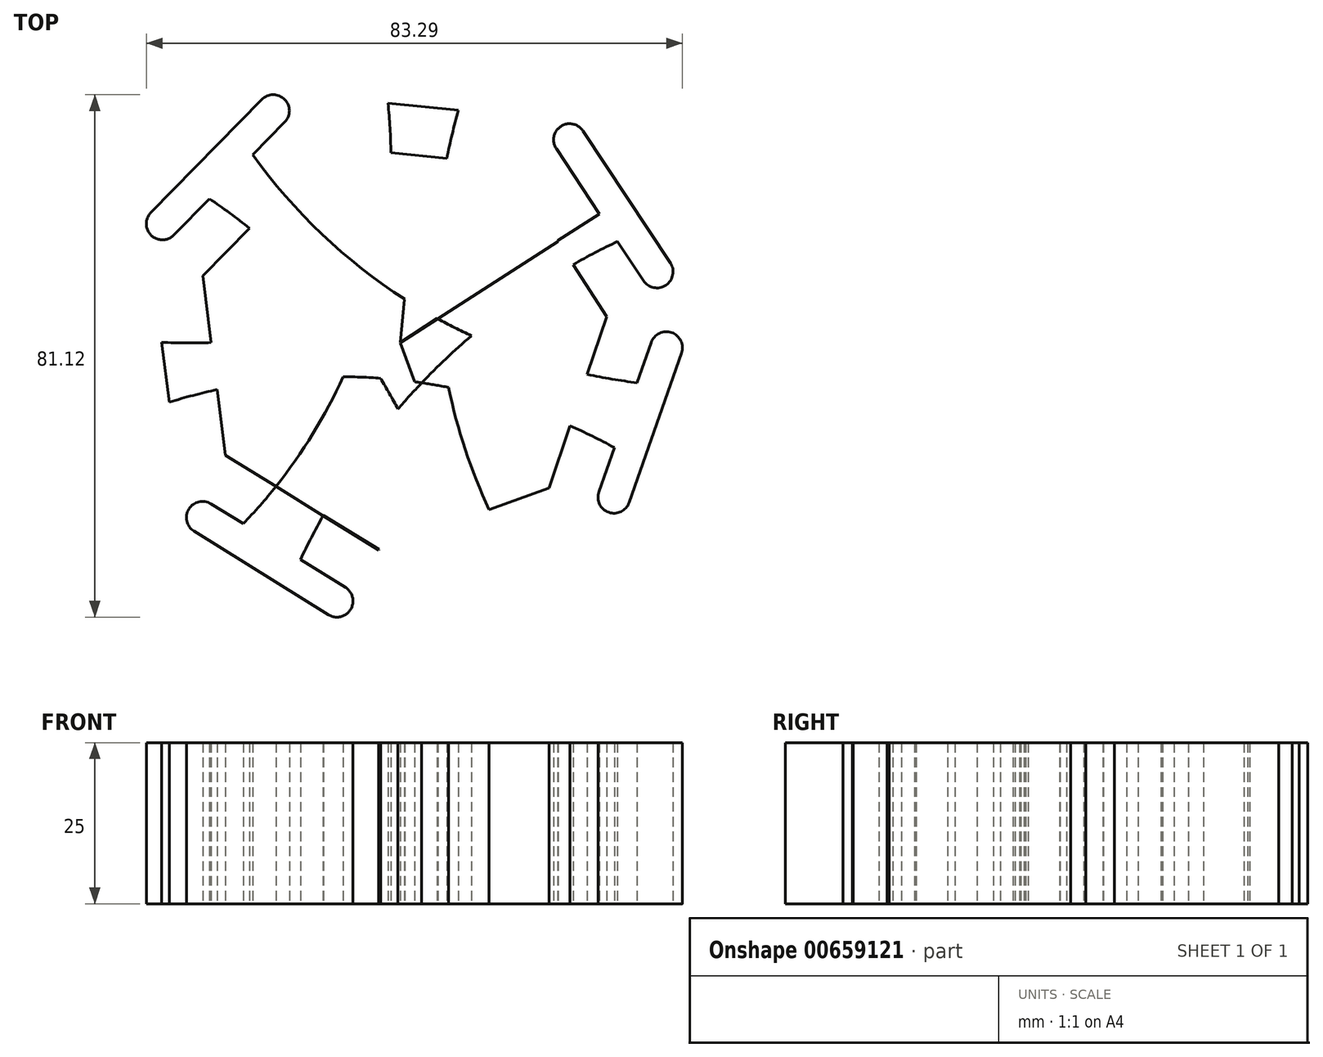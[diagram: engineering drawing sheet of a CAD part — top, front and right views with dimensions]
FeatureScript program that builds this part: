
annotation { "Feature Type Name" : "Feature", "Feature Type Description" : "" }
export const myFeature = defineFeature(function(context is Context, id is Id, definition is map)
    precondition{}
    {
        {
            var Q0;
            Q0=qCreatedBy(makeId("Top.planeOp"),FACE);
            var sketch = newSketch(context, id + "F0", { "sketchPlane" : qUnion([Q0])});
            skCircle(sketch, "E0.cCircle", {"center": v(0, 0) * mm, "radius": 29.14 * mm, "construction": true});
            skLineSegment(sketch, "E0.0", {"start": v(16.9, 27.58) * mm, "end": v(32.1, 3.99) * mm});
            skLineSegment(sketch, "E0.1", {"start": v(32.1, 3.99) * mm, "end": v(23.12, -22.6) * mm});
            skLineSegment(sketch, "E0.2", {"start": v(23.12, -22.6) * mm, "end": v(-3.25, -32.17) * mm});
            skLineSegment(sketch, "E0.3", {"start": v(-3.25, -32.17) * mm, "end": v(-27.18, -17.52) * mm});
            skLineSegment(sketch, "E0.4", {"start": v(-27.18, -17.52) * mm, "end": v(-30.64, 10.33) * mm});
            skLineSegment(sketch, "E0.5", {"start": v(-30.64, 10.33) * mm, "end": v(-11.03, 30.4) * mm});
            skLineSegment(sketch, "E0.6", {"start": v(-11.03, 30.4) * mm, "end": v(16.9, 27.58) * mm});
            skPoint(sketch, "E0.0.midPoint", {"position": v(24.5, 15.78) * mm});
            skLineSegment(sketch, "E1", {"start": v(23.12, -22.6) * mm, "end": v(27.6, -9.3) * mm});
            skLineSegment(sketch, "E2", {"start": v(-3.25, -32.17) * mm, "end": v(23.12, -22.6) * mm});
            skLineSegment(sketch, "E3", {"start": v(0, 0) * mm, "end": v(2.93, 28.99) * mm});
            skLineSegment(sketch, "E4", {"start": v(2.93, 28.99) * mm, "end": v(3.94, 38.94) * mm});
            skLineSegment(sketch, "E5.0", {"start": v(-7.82, 40.24) * mm, "end": v(16.63, 37.77) * mm});
            skArc(sketch, "E6.0.startCap", {"start": v(-8.07, 37.75) * mm, "mid": v(-10.3, 40.5) * mm, "end": v(-7.56, 42.73) * mm});
            skArc(sketch, "E6.0.endCap", {"start": v(16.89, 40.25) * mm, "mid": v(19.12, 37.51) * mm, "end": v(16.38, 35.28) * mm});
            skLineSegment(sketch, "E6.0.left", {"start": v(-7.56, 42.73) * mm, "end": v(16.89, 40.25) * mm});
            skLineSegment(sketch, "E6.0.right", {"start": v(-8.07, 37.75) * mm, "end": v(16.38, 35.28) * mm});
            skLineSegment(sketch, "E7.MirrorCS", {"start": v(-17.93, 34.19) * mm, "end": v(-35.15, 16.66) * mm});
            skLineSegment(sketch, "E8.MirrorCS", {"start": v(-20.78, 20.42) * mm, "end": v(-27.92, 27.43) * mm});
            skArc(sketch, "E9.MirrorCS", {"start": v(-38.72, 20.16) * mm, "mid": v(-38.68, 16.63) * mm, "end": v(-35.15, 16.66) * mm});
            skLineSegment(sketch, "E10.MirrorCS", {"start": v(-21.5, 37.7) * mm, "end": v(-38.72, 20.16) * mm});
            skLineSegment(sketch, "E11.MirrorCS", {"start": v(-19.7, 35.94) * mm, "end": v(-36.93, 18.41) * mm});
            skArc(sketch, "E12.MirrorCS", {"start": v(-17.93, 34.19) * mm, "mid": v(-17.96, 37.72) * mm, "end": v(-21.5, 37.7) * mm});
            skLineSegment(sketch, "E13", {"start": v(-20.78, 20.42) * mm, "end": v(0, 0) * mm});
            skLineSegment(sketch, "E14", {"start": v(0, 0) * mm, "end": v(37.25, -12.56) * mm});
            skArc(sketch, "E15.MirrorCS", {"start": v(-43.02, 7.4) * mm, "mid": v(-40.85, 10.2) * mm, "end": v(-38.06, 8.03) * mm});
            skLineSegment(sketch, "E16.MirrorCS", {"start": v(-34.97, -16.35) * mm, "end": v(-38.06, 8.03) * mm});
            skLineSegment(sketch, "E17.MirrorCS", {"start": v(-39.93, -16.98) * mm, "end": v(-43.02, 7.4) * mm});
            skLineSegment(sketch, "E18.MirrorCS", {"start": v(-28.9, -3.66) * mm, "end": v(-38.82, -4.92) * mm});
            skLineSegment(sketch, "E19.MirrorCS", {"start": v(-37.45, -16.67) * mm, "end": v(-40.54, 7.71) * mm});
            skArc(sketch, "E20.MirrorCS", {"start": v(-34.97, -16.35) * mm, "mid": v(-37.13, -19.15) * mm, "end": v(-39.93, -16.98) * mm});
            skLineSegment(sketch, "E21", {"start": v(-28.9, -3.66) * mm, "end": v(0, 0) * mm});
            skArc(sketch, "E22.MirrorCS", {"start": v(-11.15, -42.3) * mm, "mid": v(-7.7, -41.5) * mm, "end": v(-8.5, -38.06) * mm});
            skLineSegment(sketch, "E23.MirrorCS", {"start": v(-27.18, -17.52) * mm, "end": v(-3.32, -32.28) * mm});
            skLineSegment(sketch, "E24.MirrorCS", {"start": v(-15.31, -24.86) * mm, "end": v(-20.6, -33.35) * mm});
            skArc(sketch, "E25.MirrorCS", {"start": v(-29.38, -25.07) * mm, "mid": v(-32.82, -25.88) * mm, "end": v(-32.02, -29.32) * mm});
            skLineSegment(sketch, "E26.MirrorCS", {"start": v(-29.38, -25.07) * mm, "end": v(-8.5, -38.06) * mm});
            skLineSegment(sketch, "E27.MirrorCS", {"start": v(-32.02, -29.32) * mm, "end": v(-11.15, -42.3) * mm});
            skLineSegment(sketch, "E28.MirrorCS", {"start": v(-30.7, -27.2) * mm, "end": v(-9.83, -40.18) * mm});
            skLineSegment(sketch, "E29", {"start": v(-15.31, -24.86) * mm, "end": v(0, 0) * mm});
            skLineSegment(sketch, "E30", {"start": v(-3.32, -32.28) * mm, "end": v(-3.3, -32.14) * mm});
            skArc(sketch, "E31.MirrorCS", {"start": v(23.76, -30.45) * mm, "mid": v(26.97, -31.93) * mm, "end": v(25.5, -35.14) * mm});
            skLineSegment(sketch, "E32.MirrorCS", {"start": v(23.76, -30.45) * mm, "end": v(0.72, -39) * mm});
            skLineSegment(sketch, "E33.MirrorCS", {"start": v(10.03, -27.42) * mm, "end": v(13.5, -36.8) * mm});
            skLineSegment(sketch, "E34.MirrorCS", {"start": v(24.63, -32.8) * mm, "end": v(1.58, -41.33) * mm});
            skLineSegment(sketch, "E35.MirrorCS", {"start": v(25.5, -35.14) * mm, "end": v(2.45, -43.68) * mm});
            skArc(sketch, "E36.MirrorCS", {"start": v(2.45, -43.68) * mm, "mid": v(-0.76, -42.2) * mm, "end": v(0.72, -39) * mm});
            skLineSegment(sketch, "E37", {"start": v(0, 0) * mm, "end": v(10.03, -27.42) * mm});
            skLineSegment(sketch, "E38", {"start": v(0, 0) * mm, "end": v(0.05, -0.05) * mm});
            skLineSegment(sketch, "E39.MirrorCS", {"start": v(33.23, -24.04) * mm, "end": v(41.36, -0.85) * mm});
            skLineSegment(sketch, "E40.MirrorCS", {"start": v(35.59, -24.87) * mm, "end": v(43.72, -1.68) * mm});
            skLineSegment(sketch, "E41.MirrorCS", {"start": v(30.87, -23.22) * mm, "end": v(39, -0.02) * mm});
            skArc(sketch, "E42.MirrorCS", {"start": v(43.72, -1.68) * mm, "mid": v(42.18, 1.5) * mm, "end": v(39, -0.02) * mm});
            skArc(sketch, "E43.MirrorCS", {"start": v(30.87, -23.22) * mm, "mid": v(32.4, -26.4) * mm, "end": v(35.59, -24.87) * mm});
            skLineSegment(sketch, "E44.trimOffspring", {"start": v(27.6, -9.3) * mm, "end": v(0, 0) * mm});
            skLineSegment(sketch, "E45", {"start": v(0, 0) * mm, "end": v(0.16, 0.02) * mm});
            skPoint(sketch, "E46.orphan", {"position": v(37.03, -12.85) * mm});
            skPoint(sketch, "E47.MirrorCS.start.orphan", {"position": v(27.6, -9.54) * mm});
            skLineSegment(sketch, "E48.MirrorCS", {"start": v(24.5, 15.78) * mm, "end": v(0, 0) * mm});
            skLineSegment(sketch, "E49.MirrorCS", {"start": v(32.1, 3.99) * mm, "end": v(16.9, 27.58) * mm});
            skPoint(sketch, "E50.MirrorP", {"position": v(24.42, 16) * mm});
            skLineSegment(sketch, "E51.MirrorCS", {"start": v(0, 0) * mm, "end": v(33.05, 21.3) * mm});
            skLineSegment(sketch, "E52.MirrorCS", {"start": v(28.42, 32.82) * mm, "end": v(41.98, 12.32) * mm});
            skArc(sketch, "E53.MirrorCS", {"start": v(24.25, 30.06) * mm, "mid": v(24.95, 33.53) * mm, "end": v(28.42, 32.82) * mm});
            skLineSegment(sketch, "E54.MirrorCS", {"start": v(26.33, 31.44) * mm, "end": v(39.9, 10.94) * mm});
            skLineSegment(sketch, "E55.MirrorCS", {"start": v(24.25, 30.06) * mm, "end": v(37.8, 9.56) * mm});
            skPoint(sketch, "E56.MirrorP", {"position": v(32.76, 21.52) * mm});
            skArc(sketch, "E57.MirrorCS", {"start": v(41.98, 12.32) * mm, "mid": v(41.27, 8.86) * mm, "end": v(37.8, 9.56) * mm});
            skLineSegment(sketch, "E58.trimOffspring", {"start": v(24.56, 15.67) * mm, "end": v(0, -0.1) * mm});
            skLineSegment(sketch, "E59.trimOffspring", {"start": v(24.56, 15.67) * mm, "end": v(33.13, 21.16) * mm});
            skPoint(sketch, "E60.orphan", {"position": v(-49.4, 16.66) * mm});
            skLineSegment(sketch, "E61.trimOffspring", {"start": v(-0.09, -0.14) * mm, "end": v(0.16, 0.02) * mm});
            skPoint(sketch, "E62.orphan", {"position": v(-43.83, -28.24) * mm});
            skLineSegment(sketch, "E63.trimOffspring", {"start": v(0, -0.1) * mm, "end": v(0, 0) * mm});
            skArc(sketch, "E64", {"start": v(9.06, 36.02) * mm, "mid": v(6.22, 0.76) * mm, "end": v(17.36, -32.82) * mm});
            skArc(sketch, "E65", {"start": v(-24.39, -28.18) * mm, "mid": v(-5.91, 1.98) * mm, "end": v(-1.89, 37.13) * mm});
            skArc(sketch, "E66", {"start": v(-22.9, 29.13) * mm, "mid": v(3.23, 5.15) * mm, "end": v(36.8, -6.28) * mm});
            skPoint(sketch, "E66.endSnap0", {"position": v(18.63, -6.28) * mm});
            skArc(sketch, "E67", {"start": v(8.6, -36.07) * mm, "mid": v(-4.65, -3.06) * mm, "end": v(-29.62, 22.29) * mm});
            skArc(sketch, "E68", {"start": v(33.77, 15.67) * mm, "mid": v(4.86, -4.75) * mm, "end": v(-15.48, -33.72) * mm});
            skArc(sketch, "E69", {"start": v(-37.04, 0) * mm, "mid": v(-2.04, 5.57) * mm, "end": v(27.68, 24.88) * mm});
            skArc(sketch, "E70", {"start": v(33.27, -16.35) * mm, "mid": v(-0.58, -5.8) * mm, "end": v(-35.86, -9.3) * mm});
            skSolve(sketch);
        }
        {
            var Q0;
            {var subQ4=sQuery(id+"F0.wireOp",EDGE,"E31.MirrorCS");Q0=makeQuery(id+"F0.imprint","IMPRINT",FACE,{"disambiguationData":[TD([[makeQuery(id+"F0.imprint","IMPRINT",EDGE,{"derivedFrom":subQ4}),-1.0]])]});}
            var Q1;
            Q1=makeQuery(id+"F0.imprint","IMPRINT",FACE,{"disambiguationData":[TD([[makeQuery(id+"F0.imprint","IMPRINT",EDGE,{"derivedFrom":sQuery(id+"F0.wireOp",EDGE,"E40.MirrorCS")}),1.0]])]});
            var Q2;
            {var subQ0=sQuery(id+"F0.wireOp",EDGE,"E67");var subQ1=sQuery(id+"F0.wireOp",EDGE,"E2");var subQ2=makeQuery(id+"F0.imprint","INTERSECT",VERTEX,{"derivedFrom":[subQ1,subQ0]});Q2=makeQuery(id+"F0.imprint","IMPRINT",FACE,{"disambiguationData":[TD([[makeQuery(id+"F0.imprint","IMPRINT",EDGE,{"disambiguationData":[TD([[subQ2,-1.0]])],"derivedFrom":subQ1}),1.0]])]});}
            var Q3;
            {var subQ0=sQuery(id+"F0.wireOp",EDGE,"E0.3");var subQ1=sQuery(id+"F0.wireOp",EDGE,"E2");var subQ2=makeQuery(id+"F0.imprint","INTERSECT",VERTEX,{"derivedFrom":[subQ1,subQ0]});Q3=makeQuery(id+"F0.imprint","IMPRINT",FACE,{"disambiguationData":[TD([[makeQuery(id+"F0.imprint","IMPRINT",EDGE,{"disambiguationData":[TD([[subQ2,-1.0]])],"derivedFrom":subQ1}),1.0]])]});}
            var Q4;
            {var subQ4=sQuery(id+"F0.wireOp",EDGE,"E22.MirrorCS");Q4=makeQuery(id+"F0.imprint","IMPRINT",FACE,{"disambiguationData":[TD([[makeQuery(id+"F0.imprint","IMPRINT",EDGE,{"derivedFrom":subQ4}),1.0]])]});}
            var Q5;
            {var subQ3=sQuery(id+"F0.wireOp",EDGE,"E26.MirrorCS");var subQ5=sQuery(id+"F0.wireOp",EDGE,"E65");var subQ6=makeQuery(id+"F0.imprint","INTERSECT",VERTEX,{"derivedFrom":[subQ3,subQ5]});Q5=makeQuery(id+"F0.imprint","IMPRINT",FACE,{"disambiguationData":[TD([[makeQuery(id+"F0.imprint","IMPRINT",EDGE,{"disambiguationData":[TD([[subQ6,-1.0]])],"derivedFrom":subQ3}),1.0]])]});}
            var Q6;
            {var subQ1=sQuery(id+"F0.wireOp",EDGE,"E0.3");var subQ3=sQuery(id+"F0.wireOp",EDGE,"E65");var subQ4=makeQuery(id+"F0.imprint","INTERSECT",VERTEX,{"derivedFrom":[subQ1,subQ3]});Q6=makeQuery(id+"F0.imprint","IMPRINT",FACE,{"disambiguationData":[TD([[makeQuery(id+"F0.imprint","IMPRINT",EDGE,{"disambiguationData":[TD([[subQ4,-1.0]])],"derivedFrom":subQ3}),1.0]])]});}
            var Q7;
            {var subQ0=sQuery(id+"F0.wireOp",EDGE,"E21");var subQ5=sQuery(id+"F0.wireOp",EDGE,"E65");var subQ6=makeQuery(id+"F0.imprint","INTERSECT",VERTEX,{"derivedFrom":[subQ0,subQ5]});Q7=makeQuery(id+"F0.imprint","IMPRINT",FACE,{"disambiguationData":[TD([[makeQuery(id+"F0.imprint","IMPRINT",EDGE,{"disambiguationData":[TD([[subQ6,1.0]])],"derivedFrom":subQ5}),1.0]])]});}
            var Q8;
            {var subQ0=sQuery(id+"F0.wireOp",EDGE,"E29");var subQ1=sQuery(id+"F0.wireOp",EDGE,"E0.3");var subQ2=makeQuery(id+"F0.imprint","INTERSECT",VERTEX,{"derivedFrom":[subQ1,subQ0]});Q8=makeQuery(id+"F0.imprint","IMPRINT",FACE,{"disambiguationData":[TD([[makeQuery(id+"F0.imprint","IMPRINT",EDGE,{"disambiguationData":[TD([[subQ2,-1.0]])],"derivedFrom":subQ1}),-1.0]])]});}
            var Q9;
            {var subQ0=sQuery(id+"F0.wireOp",EDGE,"E65");var subQ1=sQuery(id+"F0.wireOp",EDGE,"E21");var subQ2=makeQuery(id+"F0.imprint","INTERSECT",VERTEX,{"derivedFrom":[subQ1,subQ0]});Q9=makeQuery(id+"F0.imprint","IMPRINT",FACE,{"disambiguationData":[TD([[makeQuery(id+"F0.imprint","IMPRINT",EDGE,{"disambiguationData":[TD([[subQ2,-1.0]])],"derivedFrom":subQ1}),-1.0]])]});}
            var Q10;
            Q10=makeQuery(id+"F0.imprint","IMPRINT",FACE,{"disambiguationData":[TD([[makeQuery(id+"F0.imprint","IMPRINT",EDGE,{"derivedFrom":sQuery(id+"F0.wireOp",EDGE,"E52.MirrorCS")}),-1.0]])]});
            var Q11;
            {var subQ0=sQuery(id+"F0.wireOp",EDGE,"E69");var subQ1=sQuery(id+"F0.wireOp",EDGE,"E0.0");var subQ2=makeQuery(id+"F0.imprint","INTERSECT",VERTEX,{"derivedFrom":[subQ1,subQ0]});Q11=makeQuery(id+"F0.imprint","IMPRINT",FACE,{"disambiguationData":[TD([[makeQuery(id+"F0.imprint","IMPRINT",EDGE,{"disambiguationData":[TD([[subQ2,-1.0]])],"derivedFrom":subQ1}),1.0]])]});}
            var Q12;
            {var subQ0=sQuery(id+"F0.wireOp",EDGE,"E69");var subQ1=sQuery(id+"F0.wireOp",EDGE,"E0.0");var subQ2=makeQuery(id+"F0.imprint","INTERSECT",VERTEX,{"derivedFrom":[subQ1,subQ0]});Q12=makeQuery(id+"F0.imprint","IMPRINT",FACE,{"disambiguationData":[TD([[makeQuery(id+"F0.imprint","IMPRINT",EDGE,{"disambiguationData":[TD([[subQ2,-1.0]])],"derivedFrom":subQ1}),-1.0]])]});}
            var Q13;
            {var subQ0=sQuery(id+"F0.wireOp",EDGE,"E66");var subQ1=sQuery(id+"F0.wireOp",EDGE,"E51.MirrorCS");var subQ2=makeQuery(id+"F0.imprint","INTERSECT",VERTEX,{"derivedFrom":[subQ1,subQ0]});Q13=makeQuery(id+"F0.imprint","IMPRINT",FACE,{"disambiguationData":[TD([[makeQuery(id+"F0.imprint","IMPRINT",EDGE,{"disambiguationData":[TD([[subQ2,-1.0]])],"derivedFrom":subQ1}),1.0]])]});}
            var Q14;
            {var subQ0=sQuery(id+"F0.wireOp",EDGE,"E70");var subQ1=sQuery(id+"F0.wireOp",EDGE,"E37");var subQ2=makeQuery(id+"F0.imprint","INTERSECT",VERTEX,{"derivedFrom":[subQ1,subQ0]});Q14=makeQuery(id+"F0.imprint","IMPRINT",FACE,{"disambiguationData":[TD([[makeQuery(id+"F0.imprint","IMPRINT",EDGE,{"disambiguationData":[TD([[subQ2,-1.0]])],"derivedFrom":subQ1}),-1.0]])]});}
            var Q15;
            {var subQ5=sQuery(id+"F0.wireOp",EDGE,"E15.MirrorCS");Q15=makeQuery(id+"F0.imprint","IMPRINT",FACE,{"disambiguationData":[TD([[makeQuery(id+"F0.imprint","IMPRINT",EDGE,{"derivedFrom":subQ5}),-1.0]])]});}
            var Q16;
            {var subQ0=sQuery(id+"F0.wireOp",EDGE,"E68");var subQ1=sQuery(id+"F0.wireOp",EDGE,"E0.3");var subQ2=makeQuery(id+"F0.imprint","INTERSECT",VERTEX,{"derivedFrom":[subQ1,subQ0]});Q16=makeQuery(id+"F0.imprint","IMPRINT",FACE,{"disambiguationData":[TD([[makeQuery(id+"F0.imprint","IMPRINT",EDGE,{"disambiguationData":[TD([[subQ2,-1.0]])],"derivedFrom":subQ1}),-1.0]])]});}
            var Q17;
            {var subQ0=sQuery(id+"F0.wireOp",EDGE,"E9.MirrorCS");Q17=makeQuery(id+"F0.imprint","IMPRINT",FACE,{"disambiguationData":[TD([[makeQuery(id+"F0.imprint","IMPRINT",EDGE,{"derivedFrom":subQ0}),1.0]])]});}
            var Q18;
            {var subQ1=sQuery(id+"F0.wireOp",EDGE,"E0.1");var subQ3=sQuery(id+"F0.wireOp",EDGE,"E66");var subQ4=makeQuery(id+"F0.imprint","INTERSECT",VERTEX,{"derivedFrom":[subQ1,subQ3]});Q18=makeQuery(id+"F0.imprint","IMPRINT",FACE,{"disambiguationData":[TD([[makeQuery(id+"F0.imprint","IMPRINT",EDGE,{"disambiguationData":[TD([[subQ4,1.0]])],"derivedFrom":subQ3}),-1.0]])]});}
            var Q19;
            {var subQ0=sQuery(id+"F0.wireOp",EDGE,"E2");var subQ1=sQuery(id+"F0.wireOp",EDGE,"E1");var subQ2=makeQuery(id+"F0.imprint","INTERSECT",VERTEX,{"derivedFrom":[subQ1,subQ0]});Q19=makeQuery(id+"F0.imprint","IMPRINT",FACE,{"disambiguationData":[TD([[makeQuery(id+"F0.imprint","IMPRINT",EDGE,{"disambiguationData":[TD([[subQ2,-1.0]])],"derivedFrom":subQ1}),1.0]])]});}
            var Q20;
            {var subQ1=sQuery(id+"F0.wireOp",EDGE,"E3");var subQ7=sQuery(id+"F0.wireOp",EDGE,"E69");var subQ9=makeQuery(id+"F0.imprint","INTERSECT",VERTEX,{"derivedFrom":[subQ1,subQ7]});Q20=makeQuery(id+"F0.imprint","IMPRINT",FACE,{"disambiguationData":[TD([[makeQuery(id+"F0.imprint","IMPRINT",EDGE,{"disambiguationData":[TD([[subQ9,-1.0]])],"derivedFrom":subQ1}),1.0]])]});}
            var Q21;
            {var subQ3=sQuery(id+"F0.wireOp",EDGE,"E66");var subQ5=sQuery(id+"F0.wireOp",EDGE,"E7.MirrorCS");var subQ6=makeQuery(id+"F0.imprint","INTERSECT",VERTEX,{"derivedFrom":[subQ5,subQ3]});Q21=makeQuery(id+"F0.imprint","IMPRINT",FACE,{"disambiguationData":[TD([[makeQuery(id+"F0.imprint","IMPRINT",EDGE,{"disambiguationData":[TD([[subQ6,-1.0]])],"derivedFrom":subQ5}),1.0]])]});}
            var Q22;
            {var subQ0=sQuery(id+"F0.wireOp",EDGE,"E0.5");var subQ1=sQuery(id+"F0.wireOp",EDGE,"E0.4");var subQ2=makeQuery(id+"F0.imprint","INTERSECT",VERTEX,{"derivedFrom":[subQ1,subQ0]});Q22=makeQuery(id+"F0.imprint","IMPRINT",FACE,{"disambiguationData":[TD([[makeQuery(id+"F0.imprint","IMPRINT",EDGE,{"disambiguationData":[TD([[subQ2,1.0]])],"derivedFrom":subQ1}),-1.0]])]});}
            var Q23;
            {var subQ1=sQuery(id+"F0.wireOp",EDGE,"E64");var subQ5=sQuery(id+"F0.wireOp",EDGE,"E58.trimOffspring");var subQ6=makeQuery(id+"F0.imprint","INTERSECT",VERTEX,{"derivedFrom":[subQ5,subQ1]});Q23=makeQuery(id+"F0.imprint","IMPRINT",FACE,{"disambiguationData":[TD([[makeQuery(id+"F0.imprint","IMPRINT",EDGE,{"disambiguationData":[TD([[subQ6,-1.0]])],"derivedFrom":subQ1}),1.0]])]});}
            var Q24;
            {var subQ0=sQuery(id+"F0.wireOp",EDGE,"E68");var subQ1=sQuery(id+"F0.wireOp",EDGE,"E44.trimOffspring");var subQ2=makeQuery(id+"F0.imprint","INTERSECT",VERTEX,{"derivedFrom":[subQ1,subQ0]});Q24=makeQuery(id+"F0.imprint","IMPRINT",FACE,{"disambiguationData":[TD([[makeQuery(id+"F0.imprint","IMPRINT",EDGE,{"disambiguationData":[TD([[subQ2,-1.0]])],"derivedFrom":subQ1}),-1.0]])]});}
            var Q25;
            {var subQ3=sQuery(id+"F0.wireOp",EDGE,"E64");var subQ5=sQuery(id+"F0.wireOp",EDGE,"E6.0.right");var subQ7=makeQuery(id+"F0.imprint","INTERSECT",VERTEX,{"derivedFrom":[subQ5,subQ3]});Q25=makeQuery(id+"F0.imprint","IMPRINT",FACE,{"disambiguationData":[TD([[makeQuery(id+"F0.imprint","IMPRINT",EDGE,{"disambiguationData":[TD([[subQ7,1.0]])],"derivedFrom":subQ5}),-1.0]])]});}
            var Q26;
            {var subQ3=sQuery(id+"F0.wireOp",EDGE,"E67");var subQ5=sQuery(id+"F0.wireOp",EDGE,"E7.MirrorCS");var subQ6=makeQuery(id+"F0.imprint","INTERSECT",VERTEX,{"derivedFrom":[subQ5,subQ3]});Q26=makeQuery(id+"F0.imprint","IMPRINT",FACE,{"disambiguationData":[TD([[makeQuery(id+"F0.imprint","IMPRINT",EDGE,{"disambiguationData":[TD([[subQ6,1.0]])],"derivedFrom":subQ5}),1.0]])]});}
            var Q27;
            {var subQ5=sQuery(id+"F0.wireOp",EDGE,"E64");var subQ6=sQuery(id+"F0.wireOp",EDGE,"E0.6");var subQ7=makeQuery(id+"F0.imprint","INTERSECT",VERTEX,{"derivedFrom":[subQ6,subQ5]});Q27=makeQuery(id+"F0.imprint","IMPRINT",FACE,{"disambiguationData":[TD([[makeQuery(id+"F0.imprint","IMPRINT",EDGE,{"disambiguationData":[TD([[subQ7,-1.0]])],"derivedFrom":subQ5}),-1.0]])]});}
            var Q28;
            {var subQ0=sQuery(id+"F0.wireOp",EDGE,"E0.0");var subQ1=sQuery(id+"F0.wireOp",EDGE,"E0.6");var subQ2=makeQuery(id+"F0.imprint","INTERSECT",VERTEX,{"derivedFrom":[subQ1,subQ0]});Q28=makeQuery(id+"F0.imprint","IMPRINT",FACE,{"disambiguationData":[TD([[makeQuery(id+"F0.imprint","IMPRINT",EDGE,{"disambiguationData":[TD([[subQ2,1.0]])],"derivedFrom":subQ1}),-1.0]])]});}
            var Q29;
            {var subQ1=sQuery(id+"F0.wireOp",EDGE,"E0.6");var subQ3=sQuery(id+"F0.wireOp",EDGE,"E65");var subQ4=makeQuery(id+"F0.imprint","INTERSECT",VERTEX,{"derivedFrom":[subQ1,subQ3]});Q29=makeQuery(id+"F0.imprint","IMPRINT",FACE,{"disambiguationData":[TD([[makeQuery(id+"F0.imprint","IMPRINT",EDGE,{"disambiguationData":[TD([[subQ4,1.0]])],"derivedFrom":subQ3}),-1.0]])]});}
            var Q30;
            {var subQ3=sQuery(id+"F0.wireOp",EDGE,"E2");var subQ7=sQuery(id+"F0.wireOp",EDGE,"E67");var subQ8=makeQuery(id+"F0.imprint","INTERSECT",VERTEX,{"derivedFrom":[subQ3,subQ7]});Q30=makeQuery(id+"F0.imprint","IMPRINT",FACE,{"disambiguationData":[TD([[makeQuery(id+"F0.imprint","IMPRINT",EDGE,{"disambiguationData":[TD([[subQ8,-1.0]])],"derivedFrom":subQ3}),-1.0]])]});}
            var Q31;
            {var subQ0=sQuery(id+"F0.wireOp",EDGE,"E68");var subQ3=sQuery(id+"F0.wireOp",EDGE,"E64");var subQ4=makeQuery(id+"F0.imprint","INTERSECT",VERTEX,{"derivedFrom":[subQ3,subQ0]});Q31=makeQuery(id+"F0.imprint","IMPRINT",FACE,{"disambiguationData":[TD([[makeQuery(id+"F0.imprint","IMPRINT",EDGE,{"disambiguationData":[TD([[subQ4,-1.0]])],"derivedFrom":subQ3}),1.0]])]});}
            var Q32;
            {var subQ3=sQuery(id+"F0.wireOp",EDGE,"E66");var subQ5=sQuery(id+"F0.wireOp",EDGE,"E41.MirrorCS");var subQ7=makeQuery(id+"F0.imprint","INTERSECT",VERTEX,{"derivedFrom":[subQ5,subQ3]});Q32=makeQuery(id+"F0.imprint","IMPRINT",FACE,{"disambiguationData":[TD([[makeQuery(id+"F0.imprint","IMPRINT",EDGE,{"disambiguationData":[TD([[subQ7,1.0]])],"derivedFrom":subQ5}),1.0]])]});}
            var Q33;
            {var subQ3=sQuery(id+"F0.wireOp",EDGE,"E69");var subQ5=sQuery(id+"F0.wireOp",EDGE,"E16.MirrorCS");var subQ6=makeQuery(id+"F0.imprint","INTERSECT",VERTEX,{"derivedFrom":[subQ5,subQ3]});Q33=makeQuery(id+"F0.imprint","IMPRINT",FACE,{"disambiguationData":[TD([[makeQuery(id+"F0.imprint","IMPRINT",EDGE,{"disambiguationData":[TD([[subQ6,1.0]])],"derivedFrom":subQ5}),-1.0]])]});}
            var Q34;
            {var subQ5=sQuery(id+"F0.wireOp",EDGE,"E65");var subQ6=sQuery(id+"F0.wireOp",EDGE,"E13");var subQ7=makeQuery(id+"F0.imprint","INTERSECT",VERTEX,{"derivedFrom":[subQ6,subQ5]});Q34=makeQuery(id+"F0.imprint","IMPRINT",FACE,{"disambiguationData":[TD([[makeQuery(id+"F0.imprint","IMPRINT",EDGE,{"disambiguationData":[TD([[subQ7,1.0]])],"derivedFrom":subQ5}),1.0]])]});}
            var Q35;
            {var subQ1=sQuery(id+"F0.wireOp",EDGE,"E6.0.startCap");Q35=makeQuery(id+"F0.imprint","IMPRINT",FACE,{"disambiguationData":[TD([[makeQuery(id+"F0.imprint","IMPRINT",EDGE,{"derivedFrom":subQ1}),-1.0]])]});}
            var Q36;
            {var subQ3=sQuery(id+"F0.wireOp",EDGE,"E65");var subQ5=sQuery(id+"F0.wireOp",EDGE,"E6.0.right");var subQ6=makeQuery(id+"F0.imprint","INTERSECT",VERTEX,{"derivedFrom":[subQ5,subQ3]});Q36=makeQuery(id+"F0.imprint","IMPRINT",FACE,{"disambiguationData":[TD([[makeQuery(id+"F0.imprint","IMPRINT",EDGE,{"disambiguationData":[TD([[subQ6,-1.0]])],"derivedFrom":subQ5}),-1.0]])]});}
            var Q37;
            {var subQ0=sQuery(id+"F0.wireOp",EDGE,"E0.6");var subQ1=sQuery(id+"F0.wireOp",EDGE,"E0.5");var subQ2=makeQuery(id+"F0.imprint","INTERSECT",VERTEX,{"derivedFrom":[subQ1,subQ0]});Q37=makeQuery(id+"F0.imprint","IMPRINT",FACE,{"disambiguationData":[TD([[makeQuery(id+"F0.imprint","IMPRINT",EDGE,{"disambiguationData":[TD([[subQ2,1.0]])],"derivedFrom":subQ1}),-1.0]])]});}
            var Q38;
            {var subQ0=sQuery(id+"F0.wireOp",EDGE,"E13");var subQ5=sQuery(id+"F0.wireOp",EDGE,"E65");var subQ6=makeQuery(id+"F0.imprint","INTERSECT",VERTEX,{"derivedFrom":[subQ0,subQ5]});Q38=makeQuery(id+"F0.imprint","IMPRINT",FACE,{"disambiguationData":[TD([[makeQuery(id+"F0.imprint","IMPRINT",EDGE,{"disambiguationData":[TD([[subQ6,-1.0]])],"derivedFrom":subQ5}),1.0]])]});}
            var Q39;
            {var subQ3=sQuery(id+"F0.wireOp",EDGE,"E70");var subQ5=sQuery(id+"F0.wireOp",EDGE,"E41.MirrorCS");var subQ6=makeQuery(id+"F0.imprint","INTERSECT",VERTEX,{"derivedFrom":[subQ5,subQ3]});Q39=makeQuery(id+"F0.imprint","IMPRINT",FACE,{"disambiguationData":[TD([[makeQuery(id+"F0.imprint","IMPRINT",EDGE,{"disambiguationData":[TD([[subQ6,-1.0]])],"derivedFrom":subQ5}),1.0]])]});}
            var Q40;
            {var subQ3=sQuery(id+"F0.wireOp",EDGE,"E26.MirrorCS");var subQ5=sQuery(id+"F0.wireOp",EDGE,"E68");var subQ6=makeQuery(id+"F0.imprint","INTERSECT",VERTEX,{"derivedFrom":[subQ3,subQ5]});Q40=makeQuery(id+"F0.imprint","IMPRINT",FACE,{"disambiguationData":[TD([[makeQuery(id+"F0.imprint","IMPRINT",EDGE,{"disambiguationData":[TD([[subQ6,1.0]])],"derivedFrom":subQ3}),1.0]])]});}
            var Q41;
            {var subQ0=sQuery(id+"F0.wireOp",EDGE,"E0.0");var subQ1=sQuery(id+"F0.wireOp",EDGE,"E0.1");var subQ2=makeQuery(id+"F0.imprint","INTERSECT",VERTEX,{"derivedFrom":[subQ1,subQ0]});Q41=makeQuery(id+"F0.imprint","IMPRINT",FACE,{"disambiguationData":[TD([[makeQuery(id+"F0.imprint","IMPRINT",EDGE,{"disambiguationData":[TD([[subQ2,-1.0]])],"derivedFrom":subQ1}),-1.0]])]});}
            var Q42;
            {var subQ3=sQuery(id+"F0.wireOp",EDGE,"E68");var subQ5=sQuery(id+"F0.wireOp",EDGE,"E55.MirrorCS");var subQ6=makeQuery(id+"F0.imprint","INTERSECT",VERTEX,{"derivedFrom":[subQ5,subQ3]});Q42=makeQuery(id+"F0.imprint","IMPRINT",FACE,{"disambiguationData":[TD([[makeQuery(id+"F0.imprint","IMPRINT",EDGE,{"disambiguationData":[TD([[subQ6,1.0]])],"derivedFrom":subQ5}),-1.0]])]});}
            var Q43;
            {var subQ5=sQuery(id+"F0.wireOp",EDGE,"E2");var subQ7=sQuery(id+"F0.wireOp",EDGE,"E64");var subQ8=makeQuery(id+"F0.imprint","INTERSECT",VERTEX,{"derivedFrom":[subQ5,subQ7]});Q43=makeQuery(id+"F0.imprint","IMPRINT",FACE,{"disambiguationData":[TD([[makeQuery(id+"F0.imprint","IMPRINT",EDGE,{"disambiguationData":[TD([[subQ8,1.0]])],"derivedFrom":subQ5}),1.0]])]});}
            var Q44;
            {var subQ5=sQuery(id+"F0.wireOp",EDGE,"E2");var subQ7=sQuery(id+"F0.wireOp",EDGE,"E64");var subQ9=makeQuery(id+"F0.imprint","INTERSECT",VERTEX,{"derivedFrom":[subQ5,subQ7]});Q44=makeQuery(id+"F0.imprint","IMPRINT",FACE,{"disambiguationData":[TD([[makeQuery(id+"F0.imprint","IMPRINT",EDGE,{"disambiguationData":[TD([[subQ9,1.0]])],"derivedFrom":subQ5}),-1.0]])]});}
            var Q45;
            {var subQ3=sQuery(id+"F0.wireOp",EDGE,"E70");var subQ5=sQuery(id+"F0.wireOp",EDGE,"E16.MirrorCS");var subQ7=makeQuery(id+"F0.imprint","INTERSECT",VERTEX,{"derivedFrom":[subQ5,subQ3]});Q45=makeQuery(id+"F0.imprint","IMPRINT",FACE,{"disambiguationData":[TD([[makeQuery(id+"F0.imprint","IMPRINT",EDGE,{"disambiguationData":[TD([[subQ7,-1.0]])],"derivedFrom":subQ5}),-1.0]])]});}
            var Q46;
            {var subQ1=sQuery(id+"F0.wireOp",EDGE,"E65");var subQ5=sQuery(id+"F0.wireOp",EDGE,"E21");var subQ6=makeQuery(id+"F0.imprint","INTERSECT",VERTEX,{"derivedFrom":[subQ5,subQ1]});Q46=makeQuery(id+"F0.imprint","IMPRINT",FACE,{"disambiguationData":[TD([[makeQuery(id+"F0.imprint","IMPRINT",EDGE,{"disambiguationData":[TD([[subQ6,-1.0]])],"derivedFrom":subQ1}),1.0]])]});}
            var Q47;
            {var subQ0=sQuery(id+"F0.wireOp",EDGE,"E67");var subQ1=sQuery(id+"F0.wireOp",EDGE,"E65");var subQ2=makeQuery(id+"F0.imprint","INTERSECT",VERTEX,{"derivedFrom":[subQ1,subQ0]});Q47=makeQuery(id+"F0.imprint","IMPRINT",FACE,{"disambiguationData":[TD([[makeQuery(id+"F0.imprint","IMPRINT",EDGE,{"disambiguationData":[TD([[subQ2,-1.0]])],"derivedFrom":subQ1}),1.0]])]});}
            var Q48;
            {var subQ0=sQuery(id+"F0.wireOp",EDGE,"E64");var subQ1=sQuery(id+"F0.wireOp",EDGE,"E44.trimOffspring");var subQ2=makeQuery(id+"F0.imprint","INTERSECT",VERTEX,{"derivedFrom":[subQ1,subQ0]});Q48=makeQuery(id+"F0.imprint","IMPRINT",FACE,{"disambiguationData":[TD([[makeQuery(id+"F0.imprint","IMPRINT",EDGE,{"disambiguationData":[TD([[subQ2,-1.0]])],"derivedFrom":subQ1}),-1.0]])]});}
            var Q49;
            {var subQ0=sQuery(id+"F0.wireOp",EDGE,"E61.trimOffspring");var subQ2=sQuery(id+"F0.wireOp",EDGE,"E37");var subQ3=makeQuery(id+"F0.imprint","INTERSECT",VERTEX,{"derivedFrom":[subQ2,subQ0]});Q49=makeQuery(id+"F0.imprint","IMPRINT",FACE,{"disambiguationData":[TD([[makeQuery(id+"F0.imprint","IMPRINT",EDGE,{"disambiguationData":[TD([[subQ3,-1.0]])],"derivedFrom":subQ2}),1.0]])]});}
            var Q50;
            {var subQ0=sQuery(id+"F0.wireOp",EDGE,"E29");var subQ5=makeQuery(id+"F0.imprint","INTERSECT",VERTEX,{"derivedFrom":[subQ0,sQuery(id+"F0.wireOp",EDGE,"E61.trimOffspring")]});Q50=makeQuery(id+"F0.imprint","IMPRINT",FACE,{"disambiguationData":[TD([[makeQuery(id+"F0.imprint","IMPRINT",EDGE,{"disambiguationData":[TD([[subQ5,1.0]])],"derivedFrom":subQ0}),1.0]])]});}
            var Q51;
            {var subQ0=sQuery(id+"F0.wireOp",EDGE,"E65");var subQ1=sQuery(id+"F0.wireOp",EDGE,"E21");var subQ2=makeQuery(id+"F0.imprint","INTERSECT",VERTEX,{"derivedFrom":[subQ1,subQ0]});Q51=makeQuery(id+"F0.imprint","IMPRINT",FACE,{"disambiguationData":[TD([[makeQuery(id+"F0.imprint","IMPRINT",EDGE,{"disambiguationData":[TD([[subQ2,-1.0]])],"derivedFrom":subQ1}),1.0]])]});}
            var Q52;
            {var subQ0=sQuery(id+"F0.wireOp",EDGE,"E67");var subQ3=sQuery(id+"F0.wireOp",EDGE,"E65");var subQ4=makeQuery(id+"F0.imprint","INTERSECT",VERTEX,{"derivedFrom":[subQ3,subQ0]});Q52=makeQuery(id+"F0.imprint","IMPRINT",FACE,{"disambiguationData":[TD([[makeQuery(id+"F0.imprint","IMPRINT",EDGE,{"disambiguationData":[TD([[subQ4,-1.0]])],"derivedFrom":subQ3}),-1.0]])]});}
            var Q53;
            {var subQ0=sQuery(id+"F0.wireOp",EDGE,"E65");var subQ1=sQuery(id+"F0.wireOp",EDGE,"E13");var subQ2=makeQuery(id+"F0.imprint","INTERSECT",VERTEX,{"derivedFrom":[subQ1,subQ0]});Q53=makeQuery(id+"F0.imprint","IMPRINT",FACE,{"disambiguationData":[TD([[makeQuery(id+"F0.imprint","IMPRINT",EDGE,{"disambiguationData":[TD([[subQ2,-1.0]])],"derivedFrom":subQ1}),-1.0]])]});}
            var Q54;
            {var subQ0=sQuery(id+"F0.wireOp",EDGE,"E61.trimOffspring");var subQ4=sQuery(id+"F0.wireOp",EDGE,"E29");var subQ5=makeQuery(id+"F0.imprint","INTERSECT",VERTEX,{"derivedFrom":[subQ4,subQ0]});Q54=makeQuery(id+"F0.imprint","IMPRINT",FACE,{"disambiguationData":[TD([[makeQuery(id+"F0.imprint","IMPRINT",EDGE,{"disambiguationData":[TD([[subQ5,1.0]])],"derivedFrom":subQ4}),-1.0]])]});}
            var Q55;
            {var subQ1=sQuery(id+"F0.wireOp",EDGE,"E3");var subQ3=sQuery(id+"F0.wireOp",EDGE,"E69");var subQ4=makeQuery(id+"F0.imprint","INTERSECT",VERTEX,{"derivedFrom":[subQ1,subQ3]});Q55=makeQuery(id+"F0.imprint","IMPRINT",FACE,{"disambiguationData":[TD([[makeQuery(id+"F0.imprint","IMPRINT",EDGE,{"disambiguationData":[TD([[subQ4,1.0]])],"derivedFrom":subQ3}),-1.0]])]});}
            var Q56;
            {var subQ0=sQuery(id+"F0.wireOp",EDGE,"E51.MirrorCS");var subQ5=sQuery(id+"F0.wireOp",EDGE,"E66");var subQ6=makeQuery(id+"F0.imprint","INTERSECT",VERTEX,{"derivedFrom":[subQ0,subQ5]});Q56=makeQuery(id+"F0.imprint","IMPRINT",FACE,{"disambiguationData":[TD([[makeQuery(id+"F0.imprint","IMPRINT",EDGE,{"disambiguationData":[TD([[subQ6,1.0]])],"derivedFrom":subQ5}),-1.0]])]});}
            var Q57;
            {var subQ0=sQuery(id+"F0.wireOp",EDGE,"E68");var subQ1=sQuery(id+"F0.wireOp",EDGE,"E64");var subQ2=makeQuery(id+"F0.imprint","INTERSECT",VERTEX,{"derivedFrom":[subQ1,subQ0]});Q57=makeQuery(id+"F0.imprint","IMPRINT",FACE,{"disambiguationData":[TD([[makeQuery(id+"F0.imprint","IMPRINT",EDGE,{"disambiguationData":[TD([[subQ2,-1.0]])],"derivedFrom":subQ1}),-1.0]])]});}
            var Q58;
            {var subQ0=sQuery(id+"F0.wireOp",EDGE,"E64");var subQ1=sQuery(id+"F0.wireOp",EDGE,"E58.trimOffspring");var subQ2=makeQuery(id+"F0.imprint","INTERSECT",VERTEX,{"derivedFrom":[subQ1,subQ0]});Q58=makeQuery(id+"F0.imprint","IMPRINT",FACE,{"disambiguationData":[TD([[makeQuery(id+"F0.imprint","IMPRINT",EDGE,{"disambiguationData":[TD([[subQ2,-1.0]])],"derivedFrom":subQ1}),1.0]])]});}
            var Q59;
            {var subQ0=sQuery(id+"F0.wireOp",EDGE,"E70");var subQ1=sQuery(id+"F0.wireOp",EDGE,"E37");var subQ2=makeQuery(id+"F0.imprint","INTERSECT",VERTEX,{"derivedFrom":[subQ1,subQ0]});Q59=makeQuery(id+"F0.imprint","IMPRINT",FACE,{"disambiguationData":[TD([[makeQuery(id+"F0.imprint","IMPRINT",EDGE,{"disambiguationData":[TD([[subQ2,-1.0]])],"derivedFrom":subQ1}),1.0]])]});}
            var Q60;
            {var subQ0=sQuery(id+"F0.wireOp",EDGE,"E30");Q60=makeQuery(id+"F0.imprint","IMPRINT",FACE,{"disambiguationData":[TD([[makeQuery(id+"F0.imprint","IMPRINT",EDGE,{"derivedFrom":subQ0}),1.0]])]});}
            var Q61;
            {var subQ0=sQuery(id+"F0.wireOp",EDGE,"E23.MirrorCS");var subQ3=sQuery(id+"F0.wireOp",EDGE,"E65");var subQ5=makeQuery(id+"F0.imprint","INTERSECT",VERTEX,{"derivedFrom":[subQ0,subQ3]});Q61=makeQuery(id+"F0.imprint","IMPRINT",FACE,{"disambiguationData":[TD([[makeQuery(id+"F0.imprint","IMPRINT",EDGE,{"disambiguationData":[TD([[subQ5,-1.0]])],"derivedFrom":subQ3}),1.0]])]});}
            var Q62;
            {var subQ0=sQuery(id+"F0.wireOp",EDGE,"E29");var subQ1=sQuery(id+"F0.wireOp",EDGE,"E0.3");var subQ2=makeQuery(id+"F0.imprint","INTERSECT",VERTEX,{"derivedFrom":[subQ1,subQ0]});Q62=makeQuery(id+"F0.imprint","IMPRINT",FACE,{"disambiguationData":[TD([[makeQuery(id+"F0.imprint","IMPRINT",EDGE,{"disambiguationData":[TD([[subQ2,-1.0]])],"derivedFrom":subQ1}),1.0]])]});}
            var Q63;
            {var subQ0=sQuery(id+"F0.wireOp",EDGE,"E45");Q63=makeQuery(id+"F0.imprint","IMPRINT",FACE,{"disambiguationData":[TD([[makeQuery(id+"F0.imprint","IMPRINT",EDGE,{"derivedFrom":subQ0}),1.0]])]});}
            var Q64;
            {var subQ0=sQuery(id+"F0.wireOp",EDGE,"E68");var subQ1=sQuery(id+"F0.wireOp",EDGE,"E0.3");var subQ2=makeQuery(id+"F0.imprint","INTERSECT",VERTEX,{"derivedFrom":[subQ1,subQ0]});Q64=makeQuery(id+"F0.imprint","IMPRINT",FACE,{"disambiguationData":[TD([[makeQuery(id+"F0.imprint","IMPRINT",EDGE,{"disambiguationData":[TD([[subQ2,-1.0]])],"derivedFrom":subQ1}),1.0]])]});}
            var Q65;
            {var subQ0=sQuery(id+"F0.wireOp",EDGE,"E69");var subQ1=sQuery(id+"F0.wireOp",EDGE,"E3");var subQ2=makeQuery(id+"F0.imprint","INTERSECT",VERTEX,{"derivedFrom":[subQ1,subQ0]});Q65=makeQuery(id+"F0.imprint","IMPRINT",FACE,{"disambiguationData":[TD([[makeQuery(id+"F0.imprint","IMPRINT",EDGE,{"disambiguationData":[TD([[subQ2,-1.0]])],"derivedFrom":subQ1}),-1.0]])]});}
            var Q66;
            {var subQ1=sQuery(id+"F0.wireOp",EDGE,"E0.0");var subQ3=sQuery(id+"F0.wireOp",EDGE,"E51.MirrorCS");var subQ4=makeQuery(id+"F0.imprint","INTERSECT",VERTEX,{"derivedFrom":[subQ1,subQ3]});Q66=makeQuery(id+"F0.imprint","IMPRINT",FACE,{"disambiguationData":[TD([[makeQuery(id+"F0.imprint","IMPRINT",EDGE,{"disambiguationData":[TD([[subQ4,1.0]])],"derivedFrom":subQ3}),-1.0]])]});}
            var Q67;
            {var subQ1=sQuery(id+"F0.wireOp",EDGE,"E0.0");var subQ3=sQuery(id+"F0.wireOp",EDGE,"E51.MirrorCS");var subQ4=makeQuery(id+"F0.imprint","INTERSECT",VERTEX,{"derivedFrom":[subQ1,subQ3]});Q67=makeQuery(id+"F0.imprint","IMPRINT",FACE,{"disambiguationData":[TD([[makeQuery(id+"F0.imprint","IMPRINT",EDGE,{"disambiguationData":[TD([[subQ4,-1.0]])],"derivedFrom":subQ3}),-1.0]])]});}
            var Q68;
            {var subQ0=sQuery(id+"F0.wireOp",EDGE,"E70");var subQ1=sQuery(id+"F0.wireOp",EDGE,"E29");var subQ2=makeQuery(id+"F0.imprint","INTERSECT",VERTEX,{"derivedFrom":[subQ1,subQ0]});Q68=makeQuery(id+"F0.imprint","IMPRINT",FACE,{"disambiguationData":[TD([[makeQuery(id+"F0.imprint","IMPRINT",EDGE,{"disambiguationData":[TD([[subQ2,-1.0]])],"derivedFrom":subQ1}),-1.0]])]});}
            var Q69;
            {var subQ0=sQuery(id+"F0.wireOp",EDGE,"E68");var subQ1=sQuery(id+"F0.wireOp",EDGE,"E44.trimOffspring");var subQ2=makeQuery(id+"F0.imprint","INTERSECT",VERTEX,{"derivedFrom":[subQ1,subQ0]});Q69=makeQuery(id+"F0.imprint","IMPRINT",FACE,{"disambiguationData":[TD([[makeQuery(id+"F0.imprint","IMPRINT",EDGE,{"disambiguationData":[TD([[subQ2,-1.0]])],"derivedFrom":subQ1}),1.0]])]});}
            var Q70;
            {var subQ0=sQuery(id+"F0.wireOp",EDGE,"E54.MirrorCS");var subQ1=sQuery(id+"F0.wireOp",EDGE,"E51.MirrorCS");var subQ2=makeQuery(id+"F0.imprint","INTERSECT",VERTEX,{"derivedFrom":[subQ1,subQ0]});Q70=makeQuery(id+"F0.imprint","IMPRINT",FACE,{"disambiguationData":[TD([[makeQuery(id+"F0.imprint","IMPRINT",EDGE,{"disambiguationData":[TD([[subQ2,1.0]])],"derivedFrom":subQ1}),-1.0]])]});}
            var Q71;
            {var subQ0=sQuery(id+"F0.wireOp",EDGE,"E66");var subQ1=sQuery(id+"F0.wireOp",EDGE,"E51.MirrorCS");var subQ2=makeQuery(id+"F0.imprint","INTERSECT",VERTEX,{"derivedFrom":[subQ1,subQ0]});Q71=makeQuery(id+"F0.imprint","IMPRINT",FACE,{"disambiguationData":[TD([[makeQuery(id+"F0.imprint","IMPRINT",EDGE,{"disambiguationData":[TD([[subQ2,-1.0]])],"derivedFrom":subQ1}),-1.0]])]});}
            var Q72;
            {var subQ0=sQuery(id+"F0.wireOp",EDGE,"E63.trimOffspring");Q72=makeQuery(id+"F0.imprint","IMPRINT",FACE,{"disambiguationData":[TD([[makeQuery(id+"F0.imprint","IMPRINT",EDGE,{"derivedFrom":subQ0}),1.0]])]});}
            var Q73;
            {var subQ0=sQuery(id+"F0.wireOp",EDGE,"E45");Q73=makeQuery(id+"F0.imprint","IMPRINT",FACE,{"disambiguationData":[TD([[makeQuery(id+"F0.imprint","IMPRINT",EDGE,{"derivedFrom":subQ0}),-1.0]])]});}
            var Q74;
            {var subQ0=sQuery(id+"F0.wireOp",EDGE,"E38");Q74=makeQuery(id+"F0.imprint","IMPRINT",FACE,{"disambiguationData":[TD([[makeQuery(id+"F0.imprint","IMPRINT",EDGE,{"derivedFrom":subQ0}),-1.0]])]});}
            var Q75;
            {var subQ0=sQuery(id+"F0.wireOp",EDGE,"E63.trimOffspring");Q75=makeQuery(id+"F0.imprint","IMPRINT",FACE,{"disambiguationData":[TD([[makeQuery(id+"F0.imprint","IMPRINT",EDGE,{"derivedFrom":subQ0}),-1.0]])]});}
            var Q76;
            {var subQ0=sQuery(id+"F0.wireOp",EDGE,"E38");Q76=makeQuery(id+"F0.imprint","IMPRINT",FACE,{"disambiguationData":[TD([[makeQuery(id+"F0.imprint","IMPRINT",EDGE,{"derivedFrom":subQ0}),1.0]])]});}
            extrude(context, id + "F1", {"entities" : qUnion([Q0, Q1, Q2, Q3, Q4, Q5, Q6, Q7, Q8, Q9, Q10, Q11, Q12, Q13, Q14, Q15, Q16, Q17, Q18, Q19, Q20, Q21, Q22, Q23, Q24, Q25, Q26, Q27, Q28, Q29, Q30, Q31, Q32, Q33, Q34, Q35, Q36, Q37, Q38, Q39, Q40, Q41, Q42, Q43, Q44, Q45, Q46, Q47, Q48, Q49, Q50, Q51, Q52, Q53, Q54, Q55, Q56, Q57, Q58, Q59, Q60, Q61, Q62, Q63, Q64, Q65, Q66, Q67, Q68, Q69, Q70, Q71, Q72, Q73, Q74, Q75, Q76]), "depth" : 25 * mm, "offsetDistance" : 25 * mm});
        }
    });
